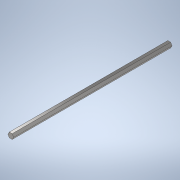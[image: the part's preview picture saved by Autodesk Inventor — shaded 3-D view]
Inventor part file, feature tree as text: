
AUTODESK INVENTOR PART (.ipt)
format: ipt  version: 2020 (Build 240168000, 168)  size: 103,936 bytes
history: native  units: in
note: dims shown in document units (in); Inventor stores cm internally (conversion verified against a paired STEP export)
features: extrude x1, sketch x1
ambient origin geometry x8: Origin, YZ Plane, XZ Plane, XY Plane, X Axis, Y Axis, Z Axis, Center Point
bodies: Solid1 (feature_tree)
feature tree (2):
  extrude  "Extrusion1"  Depth=16.0in TaperAngle=0.0deg
  sketch  "Sketch1"  dims[d0=0.5in d1=16.0in d2=0.0in]
